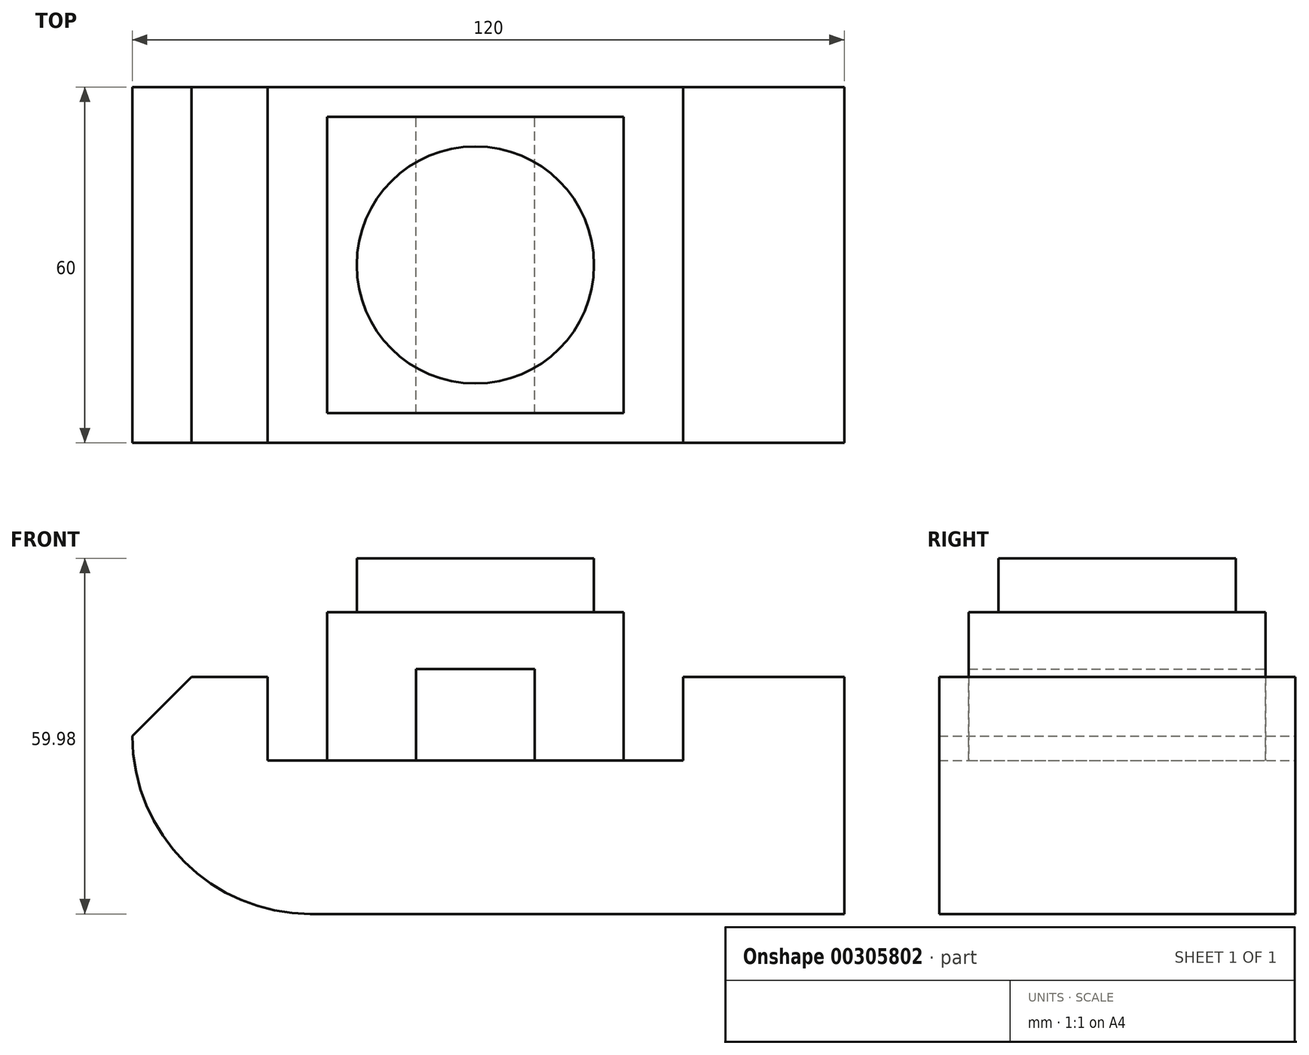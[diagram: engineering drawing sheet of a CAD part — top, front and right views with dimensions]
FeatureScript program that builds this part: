
annotation { "Feature Type Name" : "Feature", "Feature Type Description" : "" }
export const myFeature = defineFeature(function(context is Context, id is Id, definition is map)
    precondition{}
    {
        {
            var Q0;
            Q0=qCreatedBy(makeId("Front.planeOp"),FACE);
            var sketch = newSketch(context, id + "F0", { "sketchPlane" : qUnion([Q0])});
            skLineSegment(sketch, "E0.bottom", {"start": v(35, -12.95) * mm, "end": v(-35, -12.95) * mm});
            skLineSegment(sketch, "E0.top", {"start": v(35, 12.95) * mm, "end": v(-35, 12.95) * mm});
            skLineSegment(sketch, "E0.left", {"start": v(35, -12.95) * mm, "end": v(35, 12.95) * mm});
            skLineSegment(sketch, "E0.right", {"start": v(-35, -12.95) * mm, "end": v(-35, 12.95) * mm});
            skPoint(sketch, "E0.middle", {"position": v(0, 0) * mm});
            skLineSegment(sketch, "E1.bottom", {"start": v(35, -12.95) * mm, "end": v(62.18, -12.95) * mm});
            skLineSegment(sketch, "E1.top", {"start": v(35, 27.05) * mm, "end": v(62.18, 27.05) * mm});
            skLineSegment(sketch, "E1.left", {"start": v(35, -12.95) * mm, "end": v(35, 27.05) * mm});
            skLineSegment(sketch, "E1.right", {"start": v(62.18, -12.95) * mm, "end": v(62.18, 27.05) * mm});
            skLineSegment(sketch, "E2.bottom", {"start": v(-35, -12.95) * mm, "end": v(-57.82, -12.95) * mm});
            skLineSegment(sketch, "E2.top", {"start": v(-35, 27.05) * mm, "end": v(-57.82, 27.05) * mm});
            skLineSegment(sketch, "E2.left", {"start": v(-35, -12.95) * mm, "end": v(-35, 27.05) * mm});
            skLineSegment(sketch, "E2.right", {"start": v(-57.82, -12.95) * mm, "end": v(-57.82, 27.05) * mm});
            skLineSegment(sketch, "E3", {"start": v(-25, 12.95) * mm, "end": v(-25, 37.95) * mm});
            skLineSegment(sketch, "E4", {"start": v(-25, 37.95) * mm, "end": v(25, 37.95) * mm});
            skLineSegment(sketch, "E5", {"start": v(25, 37.95) * mm, "end": v(25, 12.95) * mm});
            skLineSegment(sketch, "E6", {"start": v(-10, 12.95) * mm, "end": v(-10, 28.34) * mm});
            skLineSegment(sketch, "E7", {"start": v(-10, 28.34) * mm, "end": v(10, 28.34) * mm});
            skLineSegment(sketch, "E8", {"start": v(10, 28.34) * mm, "end": v(10, 12.95) * mm});
            skLineSegment(sketch, "E9", {"start": v(-20, 37.95) * mm, "end": v(-20, 47.03) * mm});
            skLineSegment(sketch, "E10", {"start": v(-20, 47.03) * mm, "end": v(20, 47.03) * mm});
            skLineSegment(sketch, "E11", {"start": v(20, 47.03) * mm, "end": v(20, 37.95) * mm});
            skSolve(sketch);
        }
        {
            var Q0;
            {var subQ3=sQuery(id+"F0.wireOp",EDGE,"E2.bottom");Q0=makeQuery(id+"F0.imprint","IMPRINT",FACE,{"disambiguationData":[TD([[makeQuery(id+"F0.imprint","IMPRINT",EDGE,{"derivedFrom":subQ3}),-1.0]])]});}
            var Q1;
            {var subQ5=sQuery(id+"F0.wireOp",EDGE,"E0.bottom");Q1=makeQuery(id+"F0.imprint","IMPRINT",FACE,{"disambiguationData":[TD([[makeQuery(id+"F0.imprint","IMPRINT",EDGE,{"derivedFrom":subQ5}),-1.0]])]});}
            var Q2;
            {var subQ3=sQuery(id+"F0.wireOp",EDGE,"E1.bottom");Q2=makeQuery(id+"F0.imprint","IMPRINT",FACE,{"disambiguationData":[TD([[makeQuery(id+"F0.imprint","IMPRINT",EDGE,{"derivedFrom":subQ3}),1.0]])]});}
            extrude(context, id + "F1", {"entities" : qUnion([Q0, Q1, Q2]), "endBound" : BoundingType.SYMMETRIC, "depth" : 60 * mm});
        }
        {
            var Q0;
            {var subQ0=sQuery(id+"F0.wireOp",EDGE,"E3");Q0=makeQuery(id+"F0.imprint","IMPRINT",FACE,{"disambiguationData":[TD([[makeQuery(id+"F0.imprint","IMPRINT",EDGE,{"derivedFrom":subQ0}),-1.0]])]});}
            extrude(context, id + "F2", {"entities" : qUnion([Q0]), "operationType" : NewBodyOperationType.ADD, "endBound" : BoundingType.SYMMETRIC, "depth" : 50 * mm});
        }
        {
            var Q0;
            {var subQ0=sQuery(id+"F0.wireOp",EDGE,"E9");Q0=makeQuery(id+"F0.imprint","IMPRINT",FACE,{"disambiguationData":[TD([[makeQuery(id+"F0.imprint","IMPRINT",EDGE,{"derivedFrom":subQ0}),-1.0]])]});}
            extrude(context, id + "F3", {"entities" : qUnion([Q0]), "operationType" : NewBodyOperationType.ADD, "endBound" : BoundingType.SYMMETRIC, "depth" : 40 * mm});
        }
        {
            var Q0;
            Q0=makeQuery(id+"F1.opExtrude","SWEPT_EDGE",EDGE,{"disambiguationData":[OSD([sQuery(id+"F0.wireOp",EDGE,"E2.bottom"),sQuery(id+"F0.wireOp",EDGE,"E2.right")])]});
            fillet(context, id + "F4", {"entities" : qUnion([Q0]), "radius" : 30 * mm, "tangentPropagation" : true, "allowEdgeOverflow" : false});
        }
        {
            var Q0;
            Q0=makeQuery(id+"F1.opExtrude","SWEPT_EDGE",EDGE,{"disambiguationData":[OSD([sQuery(id+"F0.wireOp",EDGE,"E2.top"),sQuery(id+"F0.wireOp",EDGE,"E2.right")])]});
            chamfer(context, id + "F5", {"entities" : qUnion([Q0]), "width" : 10 * mm, "tangentPropagation" : true});
        }
        {
            var Q0;
            Q0=makeQuery(id+"F3.opExtrude","CAP_EDGE",EDGE,{"disambiguationData":[OSD([sQuery(id+"F0.wireOp",EDGE,"E11")])],"isStart":false});
            var Q1;
            Q1=makeQuery(id+"F3.opExtrude","CAP_EDGE",EDGE,{"disambiguationData":[OSD([sQuery(id+"F0.wireOp",EDGE,"E11")])],"isStart":true});
            var Q2;
            Q2=makeQuery(id+"F3.opExtrude","CAP_EDGE",EDGE,{"disambiguationData":[OSD([sQuery(id+"F0.wireOp",EDGE,"E9")])],"isStart":false});
            var Q3;
            Q3=makeQuery(id+"F3.opExtrude","CAP_EDGE",EDGE,{"disambiguationData":[OSD([sQuery(id+"F0.wireOp",EDGE,"E9")])],"isStart":true});
            fillet(context, id + "F6", {"entities" : qUnion([Q0, Q1, Q2, Q3]), "radius" : 20 * mm, "tangentPropagation" : true, "allowEdgeOverflow" : false});
        }
    });
